# Revit family: AM 150 HDIB
name_source: partatom
category: Mechanical Equipment
units: mm (PartAtom-declared; Revit-internal decimal feet)

## family parameters
Always vertical = Yes
Cut with Voids When Loaded = No
OmniClass Number = 23.75.00.00
OmniClass Title = Climate Control (HVAC)
Part Type = Normal
Room Calculation Point = No
Round Connector Dimension = Use Diameter
Shared = No
Work Plane-Based = No

## types (1)
- AM 150 HDIB
    BMS IN = (PTS) 2x2x0,6
    BMS Out = (PTS) 2x2x0,6
    BMS Panel = (PTS) 2x2x0,6
    Condensate = 6 mm  [stored 0.019685 ft]
    Electrical connection = 1 ~ 230 V / N / PE / 50 Hz
    Exhaust Air = 125 mm
    L-C Duct Exhaust = 105 mm  [stored 0.344488 ft]
    Manufacturer = Airmaster A/S
    Max. flow rate 30 dB(A) with ePM10 50% filters = 115 m³
    Max. flow rate 30 dB(A) with ePM10 55% filters = 90 m³
    Max. flow rate 30 dB(A) with ePM10 80% filters = 85 m³
    Max. flow rate 35 dB(A) with ePM10 50% filters = 147 m³
    Max. flow rate 35 dB(A) with ePM10 55% filters = 126 m³
    Max. flow rate 35 dB(A) with ePM10 80% filters = 115 m³
    Model = AM 150 HDIB
    Network Conection = AWG 24 CAT 5e STP
    Nominal current, air handling unit = 0,3 A
    Nominal current, electrical comfort heating surface = 2,17 A
    Nominal current, electrical preheating surface = 4,35 A
    Phase 1 - Max Current = 7,97 A
    Phase 1 - Max Power Consumption = 1175 W
    R-C Duct Supply = 105 mm  [stored 0.344488 ft]
    Return Air = 125 mm  [stored 0.410105 ft]
    Suply Air In = 125 mm
    Supply Air in = 125 mm  [stored 0.410105 ft]
    T-C Duct Exhaust = 158 mm
    T-C Duct Supply = 158 mm
    Total Depth = 571 mm  [stored 1.87336 ft]
    Total Hight = 262 mm  [stored 0.85958 ft]
    Total Width = 1170 mm  [stored 3.83858 ft]
    URL = www.airmaster-as.com
    Water Heater Surface IN = 15 mm  [stored 0.0492126 ft]
    Water Heater Surface Return = 15 mm  [stored 0.0492126 ft]
    Weight (Standard Unit) = 47

note: [stored X ft] marks values corroborated as IEEE doubles in the binary element streams (Revit-internal decimal feet)

## geometry (parser evidence)
native form markers: Sweep x6
no freeform markers — native parametric forms only
